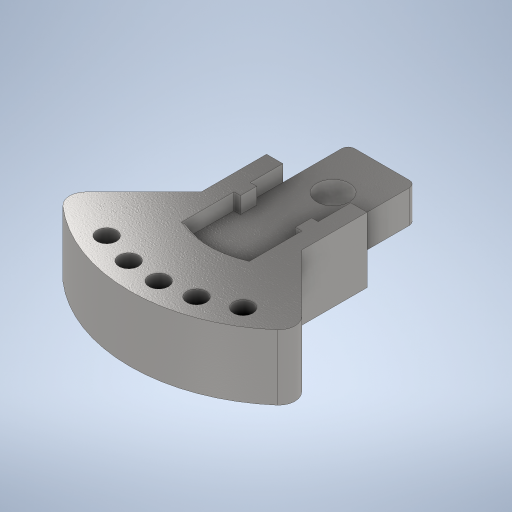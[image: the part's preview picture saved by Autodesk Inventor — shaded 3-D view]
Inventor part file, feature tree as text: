
AUTODESK INVENTOR PART (.ipt)
format: ipt  version: 2024 (Build 280153000, 153)  size: 378,368 bytes
history: native  units: mm
features: sketch x3, extrude x2, hole x2, chamfer x1, fillet x1
ambient origin geometry x8: Origin, YZ Plane, XZ Plane, XY Plane, X Axis, Y Axis, Z Axis, Center Point
bodies: Volumenkörper1 (feature_tree)
feature tree (9):
  sketch  "Skizze1"  dims[d0=90.0deg d1=5.0mm]
  extrude  "Extrusion1"  Depth=5.0mm
  extrude  "Extrusion2"  Depth=25.0mm
  hole  "Bohrung1"  [1 undecoded]
  chamfer  "Fasen1"  Distance=5.0mm
  hole  "Bohrung2"  [1 undecoded]
  fillet  "Rundung1"  Radius=30.0mm
  sketch  "Skizze2"  dims[d2=50.0mm d3=25.0mm]
  sketch  "Skizze3"  dims[d4=20.0mm d5=10.0mm d6=5.0mm d7=5.0mm d8=30.0mm d9=2.0mm d10=15.0mm d11=25.0mm d12=10.0mm d13=0.0mm d14=20.0mm d15=0.0mm d16=15.0mm d17=10.0mm d18=6.0mm d19=4.0mm d20=2.0mm d21=90.0deg d22=8.0mm d23=20.594885mm d24=1.0mm d25=2.0mm d26=45.0deg d27=10.0mm d28=10.0mm d29=10.0mm d30=10.0mm d31=6.0mm d32=6.0mm d33=4.0mm d34=2.0mm d35=90.0deg d36=8.0mm d37=20.594885mm d38=2.0mm]
note: 2 required parameter values undecoded (feature->parameter linkage not recoverable at this tier; creation-order binding heuristic only, values carry confidence <= 0.55)
